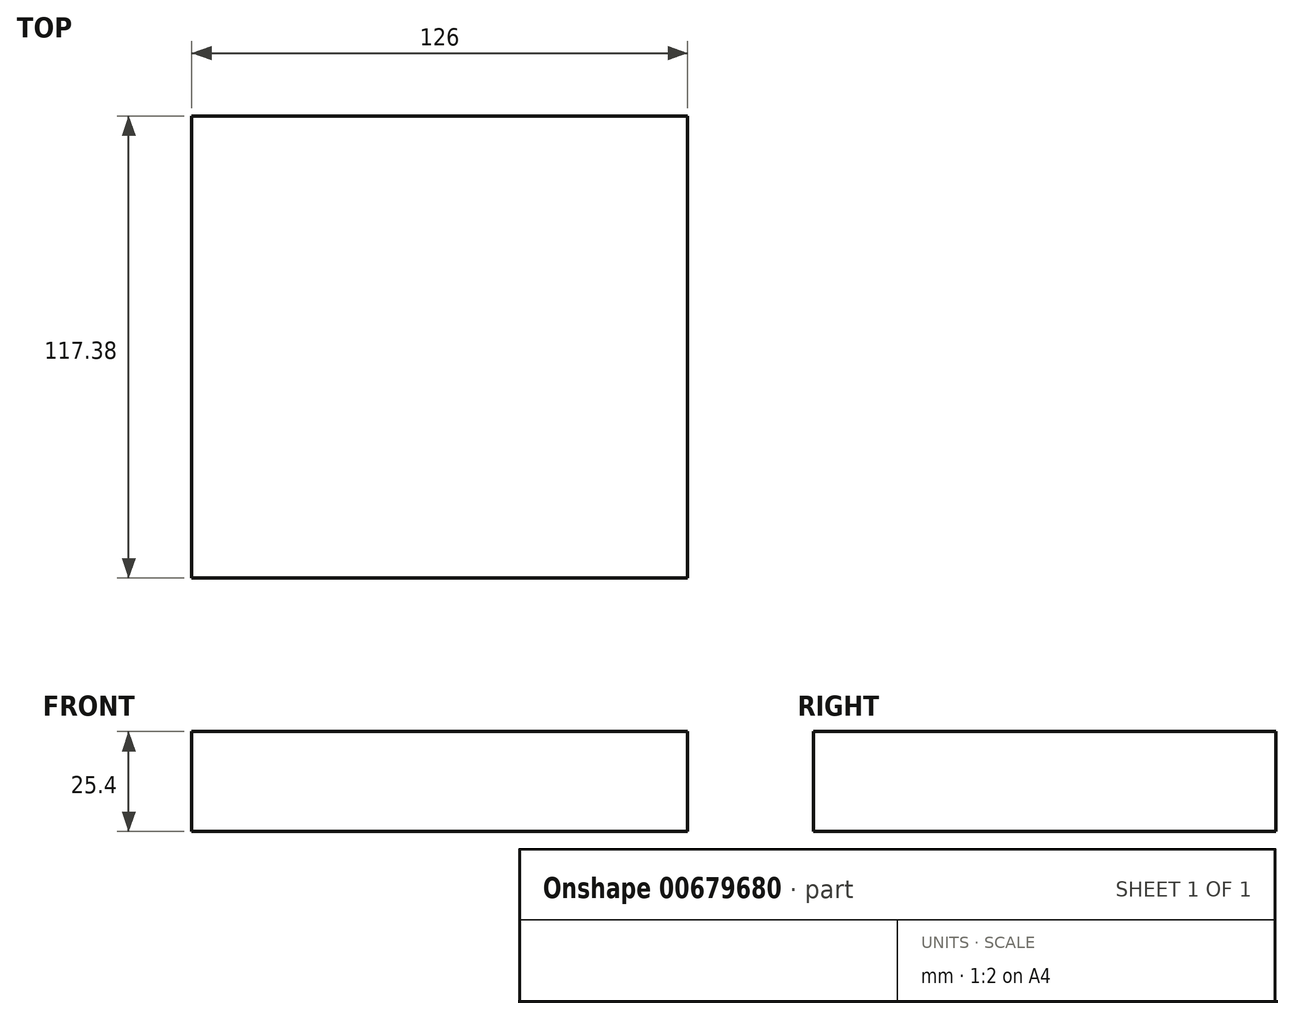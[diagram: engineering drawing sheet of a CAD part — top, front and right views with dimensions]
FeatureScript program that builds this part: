
annotation { "Feature Type Name" : "Feature", "Feature Type Description" : "" }
export const myFeature = defineFeature(function(context is Context, id is Id, definition is map)
    precondition{}
    {
        {
            var Q0;
            Q0=qCreatedBy(makeId("Top.planeOp"),FACE);
            var sketch = newSketch(context, id + "F0", { "sketchPlane" : qUnion([Q0])});
            skLineSegment(sketch, "E0.bottom", {"start": v(-62.77, -55.72) * mm, "end": v(63.23, -55.72) * mm});
            skLineSegment(sketch, "E0.top", {"start": v(-62.77, 61.66) * mm, "end": v(63.23, 61.66) * mm});
            skLineSegment(sketch, "E0.left", {"start": v(-62.77, -55.72) * mm, "end": v(-62.77, 61.66) * mm});
            skLineSegment(sketch, "E0.right", {"start": v(63.23, -55.72) * mm, "end": v(63.23, 61.66) * mm});
            skSolve(sketch);
        }
        {
            var Q0;
            Q0 = qSketchRegion(id + "F0", true);
            extrude(context, id + "F1", {"entities" : qUnion([Q0]), "depth" : 25.4 * mm, "offsetDistance" : 25.4 * mm});
        }
    });
